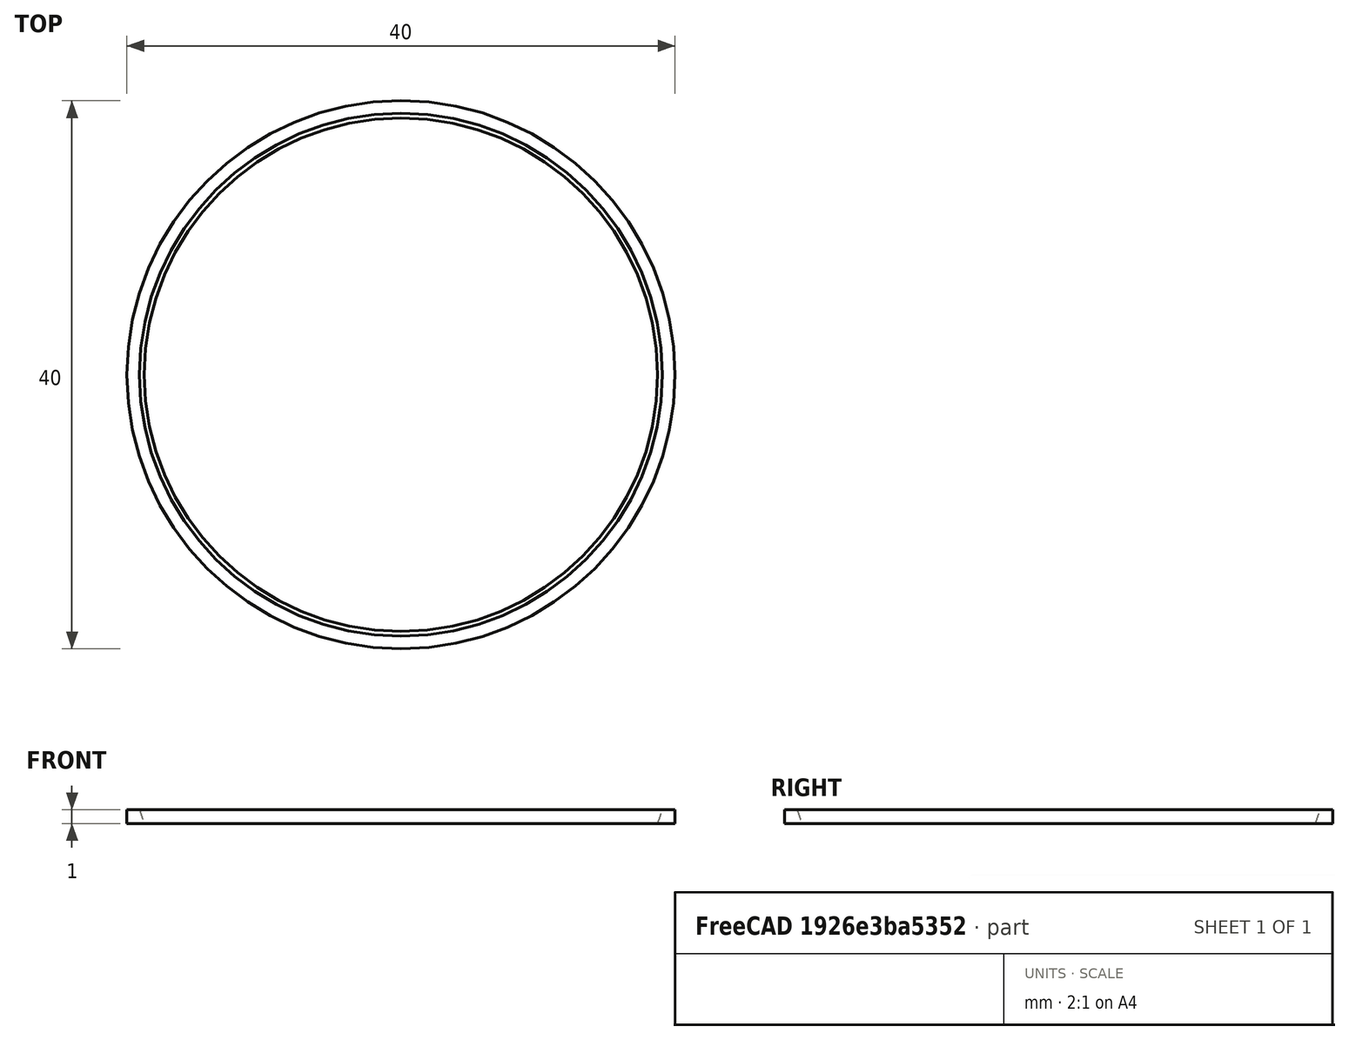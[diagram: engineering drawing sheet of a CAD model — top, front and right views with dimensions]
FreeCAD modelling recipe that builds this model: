
FCSTD DOCUMENT  (FreeCAD 0.20R29603 (Git))
Label: capsule_topper
License: All rights reserved
LicenseURL: http://en.wikipedia.org/wiki/All_rights_reserved
objects: Sketcher::SketchObject×1, PartDesign::Pad×1, PartDesign::Body×1, Part::Sphere×1, Part::Cut×1
note: 6 computed .brp shape members not serialized (recipe doc carries the construction recipe); baked Part::Feature solids carry a one-line shape summary decoded from their .brp

FEATURE [Sketcher::SketchObject] Sketch
  FullyConstrained = true
  MapMode = 5
  Support = -> [XY_Plane]
  sketch-geometry (1):
    g0: Circle CenterX=0 CenterY=0 CenterZ=0 NormalX=0 NormalY=0 NormalZ=1 AngleXU=0 Radius=20
  constraints (2):
    c: Coincident(g0,g-1)
    c: Diameter(g0) = 40
FEATURE [PartDesign::Pad] Pad
  Direction = (0,0,1)
  Length = 1
  Length2 = 10
  Profile = -> Sketch
  ReferenceAxis = -> Sketch [N_Axis]
  Type = 0
FEATURE [PartDesign::Body] Body
  Group = -> [Sketch,Pad]
  Origin = -> Origin
  Tip = -> Pad
FEATURE [Part::Sphere] Sphere  label="Сфера"
  Angle1 = -90
  Angle2 = 90
  Angle3 = 360
  AttacherType = Attacher::AttachEngine3D
  Placement = pos=(0,0,7) rot=(0,0,1;0rad)
  Radius = 20
FEATURE [Part::Cut] Cut
  Base = -> Body
  Tool = -> Sphere
